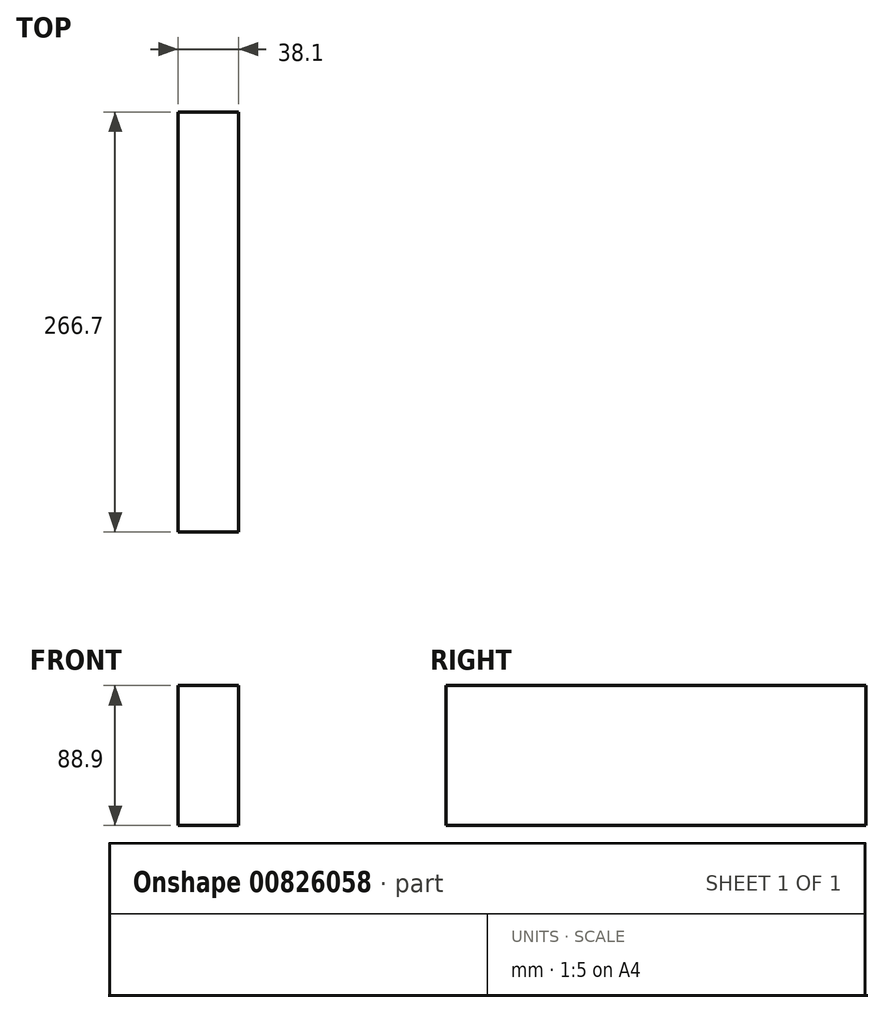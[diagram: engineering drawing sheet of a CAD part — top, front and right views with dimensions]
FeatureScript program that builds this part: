
annotation { "Feature Type Name" : "Feature", "Feature Type Description" : "" }
export const myFeature = defineFeature(function(context is Context, id is Id, definition is map)
    precondition{}
    {
        {
            var Q0;
            Q0=qCreatedBy(makeId("Front.planeOp"),FACE);
            var sketch = newSketch(context, id + "F0", { "sketchPlane" : qUnion([Q0])});
            skLineSegment(sketch, "E0.bottom", {"start": v(-19.05, 44.45) * mm, "end": v(19.05, 44.45) * mm});
            skLineSegment(sketch, "E0.top", {"start": v(-19.05, -44.45) * mm, "end": v(19.05, -44.45) * mm});
            skLineSegment(sketch, "E0.left", {"start": v(-19.05, 44.45) * mm, "end": v(-19.05, -44.45) * mm});
            skLineSegment(sketch, "E0.right", {"start": v(19.05, 44.45) * mm, "end": v(19.05, -44.45) * mm});
            skPoint(sketch, "E0.middle", {"position": v(0, 0) * mm});
            skSolve(sketch);
        }
        {
            var Q0;
            Q0=makeQuery(id+"F0.imprint","IMPRINT",FACE,{"disambiguationData":[TD([[makeQuery(id+"F0.imprint","IMPRINT",EDGE,{"derivedFrom":sQuery(id+"F0.wireOp",EDGE,"E0.bottom")}),-1.0]])]});
            extrude(context, id + "F1", {"entities" : qUnion([Q0]), "endBound" : BoundingType.SYMMETRIC, "depth" : 266.7 * mm, "offsetDistance" : 25.4 * mm});
        }
    });
